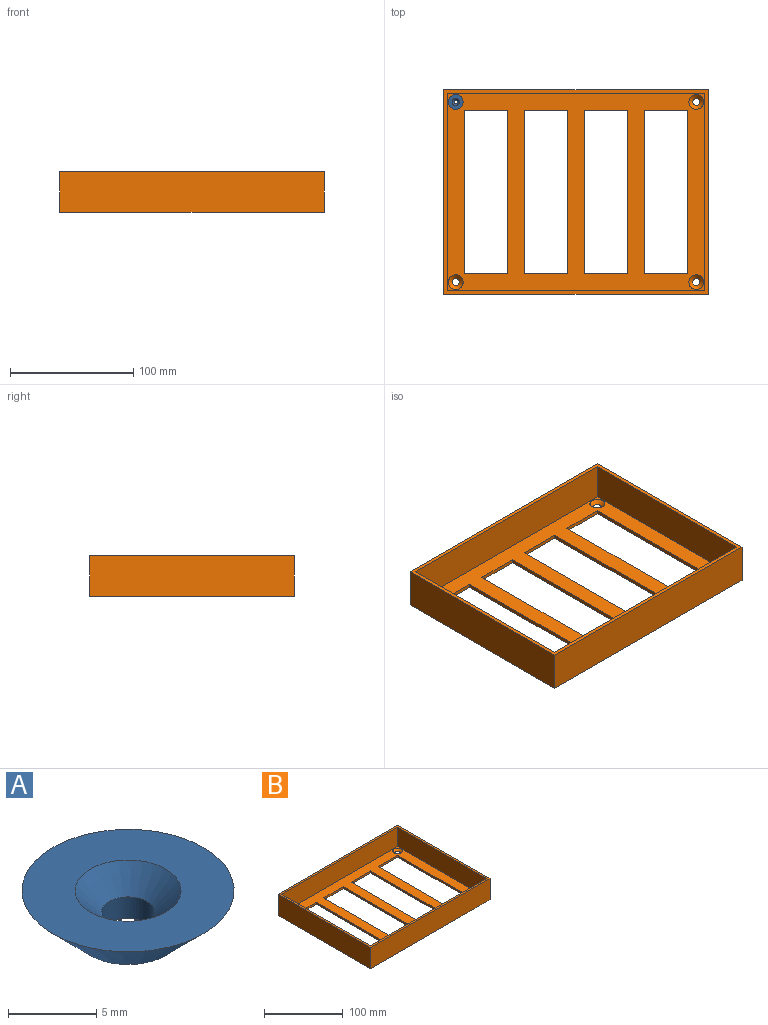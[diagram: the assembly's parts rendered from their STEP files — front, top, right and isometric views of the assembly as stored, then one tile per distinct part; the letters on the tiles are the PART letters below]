
ASSEMBLY  parts=2 mates=1
PART A: 5 faces, bbox 12x12x3 mm
  f0: plane 12x12mm, normal (0,0,1), area 84.8mm2, adj f2,f4
  f1: plane 6x6mm, normal (0,0,-1), area 21.2mm2, adj f2,f3
  f2: cone r=3mm half-angle=45deg, axis (0,0,1), area 120mm2, adj f0,f1
  f3: cylinder r=1.5mm len=3mm, axis (0,0,1), area 14.1mm2, adj f1,f4
  f4: cone r=1.5mm half-angle=45deg, axis (0,0,1), area 30mm2, adj f0,f3
PART B: 31 faces, bbox 215x166x33 mm
  f0: plane 209x160mm, normal (0,0,1), area 14451.6mm2, adj f6,f7,f8,f9,f11,f12,f13,f14
  f1: plane 215x166mm, normal (0,0,-1), area 17040.9mm2, adj f2,f3,f4,f5,f11,f12,f13,f14
  f2: plane 215x33mm, normal (0,1,0), area 7095mm2, adj f1,f3,f5,f10
  f3: plane 166x33mm, normal (-1,0,0), area 5478mm2, adj f1,f2,f4,f10
  f4: plane 215x33mm, normal (0,-1,0), area 7095mm2, adj f1,f3,f5,f10
  f5: plane 166x33mm, normal (1,0,0), area 5478mm2, adj f1,f2,f4,f10
  f6: plane 160x30mm, normal (1,0,0), area 4800mm2, adj f0,f7,f9,f10
  f7: plane 209x30mm, normal (0,-1,0), area 6270mm2, adj f0,f6,f8,f10
  f8: plane 160x30mm, normal (-1,0,0), area 4800mm2, adj f0,f7,f9,f10
  f9: plane 209x30mm, normal (0,1,0), area 6270mm2, adj f0,f6,f8,f10
  f10: plane 215x166mm, normal (0,0,1), area 2250mm2, adj f2,f3,f4,f5,f6,f7,f8,f9
  f11: plane 35x3mm, normal (0,-1,0), area 105mm2, adj f0,f1,f12,f14
  f12: plane 132.4x3mm, normal (1,0,0), area 397.2mm2, adj f0,f1,f11,f13
  f13: plane 35x3mm, normal (0,1,0), area 105mm2, adj f0,f1,f12,f14
  f14: plane 132.4x3mm, normal (-1,0,0), area 397.2mm2, adj f0,f1,f11,f13
  f15: plane 35x3mm, normal (0,-1,0), area 105mm2, adj f0,f1,f16,f18
  f16: plane 132.4x3mm, normal (1,0,0), area 397.2mm2, adj f0,f1,f15,f17
  f17: plane 35x3mm, normal (0,1,0), area 105mm2, adj f0,f1,f16,f18
  f18: plane 132.4x3mm, normal (-1,0,0), area 397.2mm2, adj f0,f1,f15,f17
  f19: plane 35x3mm, normal (0,-1,0), area 105mm2, adj f0,f1,f20,f22
  f20: plane 132.4x3mm, normal (1,0,0), area 397.2mm2, adj f0,f1,f19,f21
  f21: plane 35x3mm, normal (0,1,0), area 105mm2, adj f0,f1,f20,f22
  f22: plane 132.4x3mm, normal (-1,0,0), area 397.2mm2, adj f0,f1,f19,f21
  f23: plane 35x3mm, normal (0,-1,0), area 105mm2, adj f0,f1,f24,f26
  f24: plane 132.4x3mm, normal (1,0,0), area 397.2mm2, adj f0,f1,f23,f25
  f25: plane 35x3mm, normal (0,1,0), area 105mm2, adj f0,f1,f24,f26
  f26: plane 132.4x3mm, normal (-1,0,0), area 397.2mm2, adj f0,f1,f23,f25
  f27: cone r=3mm half-angle=45deg, axis (0,0,1), area 120mm2, adj f0,f1
  f28: cone r=3mm half-angle=45deg, axis (0,0,1), area 120mm2, adj f0,f1
  f29: cone r=3mm half-angle=45deg, axis (0,0,1), area 120mm2, adj f0,f1
  f30: cone r=3mm half-angle=45deg, axis (0,0,1), area 120mm2, adj f0,f1
PLACE A t=(-112.63,90.91,24.95)mm
PLACE B t=(-10.92,-15.73,24.7)mm
MATE fastened A.f3 <-> B.f30  axis (0,0,1) through (-114.33,90.91,24.7)mm
